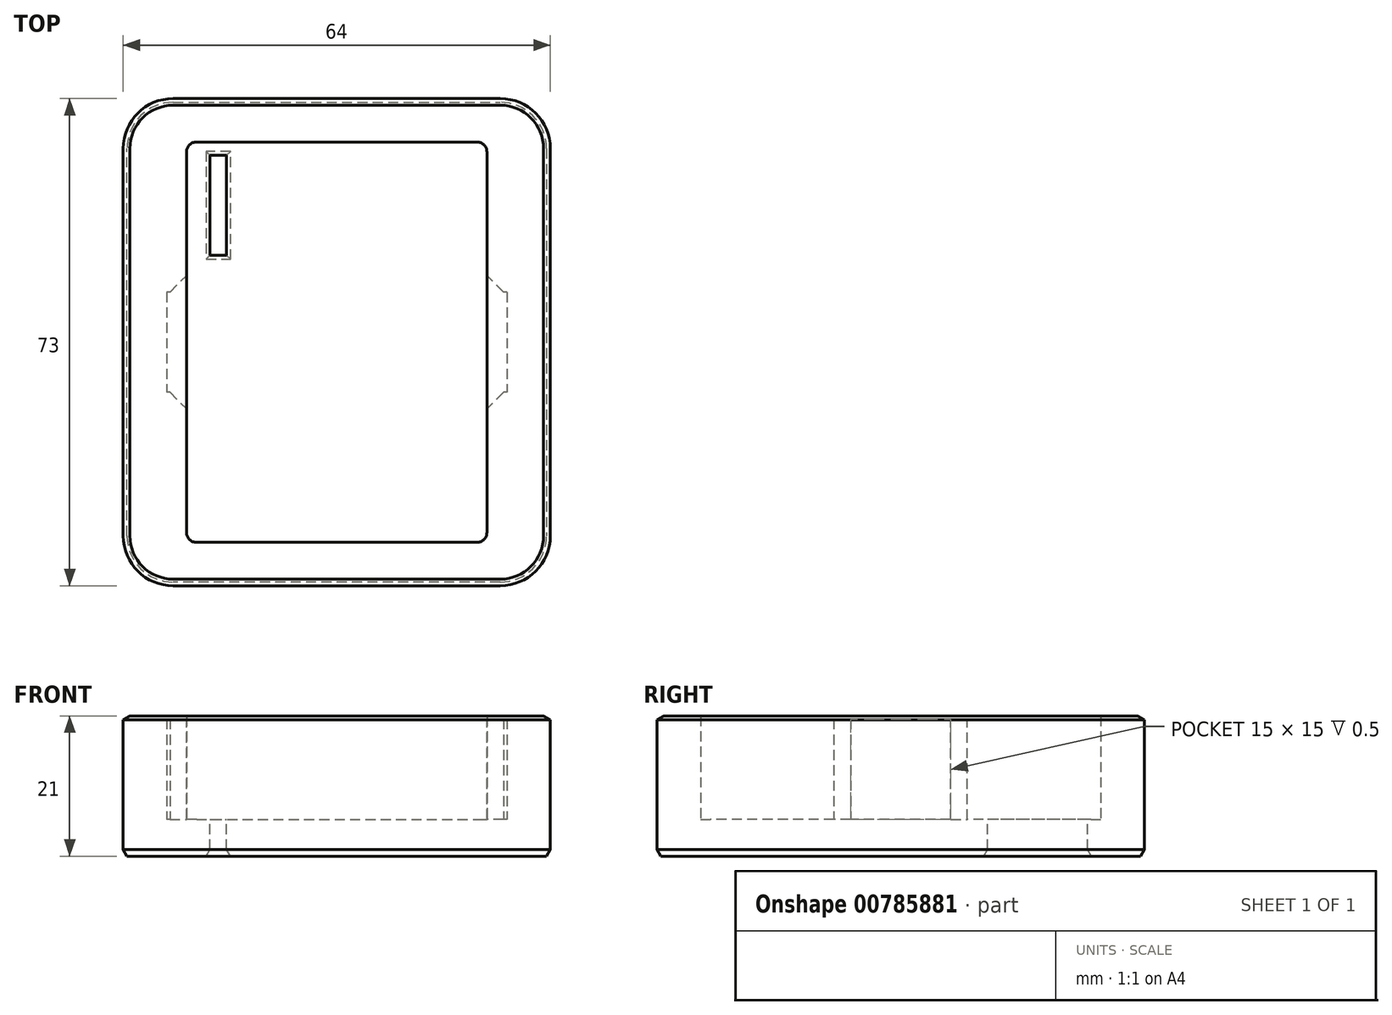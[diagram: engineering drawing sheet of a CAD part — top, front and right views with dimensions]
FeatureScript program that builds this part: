
annotation { "Feature Type Name" : "Feature", "Feature Type Description" : "" }
export const myFeature = defineFeature(function(context is Context, id is Id, definition is map)
    precondition{}
    {
        {
            var Q0;
            Q0=qCreatedBy(makeId("Top.planeOp"),FACE);
            var sketch = newSketch(context, id + "F0", { "sketchPlane" : qUnion([Q0])});
            skLineSegment(sketch, "E0.bottom", {"start": v(32, 36.5) * mm, "end": v(-32, 36.5) * mm});
            skLineSegment(sketch, "E0.top", {"start": v(32, -36.5) * mm, "end": v(-32, -36.5) * mm});
            skLineSegment(sketch, "E0.left", {"start": v(32, 36.5) * mm, "end": v(32, -36.5) * mm});
            skLineSegment(sketch, "E0.right", {"start": v(-32, 36.5) * mm, "end": v(-32, -36.5) * mm});
            skPoint(sketch, "E0.middle", {"position": v(0, 0) * mm});
            skLineSegment(sketch, "E1.bottom", {"start": v(-22.5, 30) * mm, "end": v(22.5, 30) * mm});
            skLineSegment(sketch, "E1.top", {"start": v(-22.5, -30) * mm, "end": v(22.5, -30) * mm});
            skLineSegment(sketch, "E1.left", {"start": v(-22.5, 30) * mm, "end": v(-22.5, 7.5) * mm});
            skLineSegment(sketch, "E1.right", {"start": v(22.5, 30) * mm, "end": v(22.5, 7.5) * mm});
            skLineSegment(sketch, "E2.bottom", {"start": v(25.5, 7.5) * mm, "end": v(22.5, 7.5) * mm});
            skLineSegment(sketch, "E2.top", {"start": v(25.5, -7.5) * mm, "end": v(22.5, -7.5) * mm});
            skLineSegment(sketch, "E2.left", {"start": v(25.5, 7.5) * mm, "end": v(25.5, -7.5) * mm});
            skLineSegment(sketch, "E2.right", {"start": v(-25.5, 7.5) * mm, "end": v(-25.5, -7.5) * mm});
            skLineSegment(sketch, "E3.trimOffspring", {"start": v(-22.5, 7.5) * mm, "end": v(-25.5, 7.5) * mm});
            skLineSegment(sketch, "E4.trimOffspring", {"start": v(-22.5, -7.5) * mm, "end": v(-25.5, -7.5) * mm});
            skLineSegment(sketch, "E5.trimOffspring", {"start": v(22.5, -7.5) * mm, "end": v(22.5, -30) * mm});
            skLineSegment(sketch, "E6.trimOffspring", {"start": v(-22.5, -7.5) * mm, "end": v(-22.5, -30) * mm});
            skSolve(sketch);
        }
        {
            var Q0;
            Q0=makeQuery(id+"F0.imprint","IMPRINT",FACE,{"disambiguationData":[TD([[makeQuery(id+"F0.imprint","IMPRINT",EDGE,{"derivedFrom":sQuery(id+"F0.wireOp",EDGE,"E0.bottom")}),1.0]])]});
            var Q1;
            Q1=makeQuery(id+"F0.imprint","IMPRINT",FACE,{"disambiguationData":[TD([[makeQuery(id+"F0.imprint","IMPRINT",EDGE,{"derivedFrom":sQuery(id+"F0.wireOp",EDGE,"E1.bottom")}),-1.0]])]});
            extrude(context, id + "F1", {"entities" : qUnion([Q0, Q1]), "oppositeDirection" : true, "depth" : (19 - 13.5) * mm, "offsetDistance" : 25 * mm});
        }
        {
            var Q0;
            Q0=makeQuery(id+"F0.imprint","IMPRINT",FACE,{"disambiguationData":[TD([[makeQuery(id+"F0.imprint","IMPRINT",EDGE,{"derivedFrom":sQuery(id+"F0.wireOp",EDGE,"E0.bottom")}),1.0]])]});
            extrude(context, id + "F2", {"entities" : qUnion([Q0]), "operationType" : NewBodyOperationType.ADD, "depth" : 15.5 * mm, "offsetDistance" : 25 * mm});
        }
        {
            var Q0;
            Q0=makeQuery(id+"F2.opExtrude","SWEPT_FACE",FACE,{"disambiguationData":[OSD([sQuery(id+"F0.wireOp",EDGE,"E2.right")])]});
            var sketch = newSketch(context, id + "F3", { "sketchPlane" : qUnion([Q0])});
            skLineSegment(sketch, "E7.bottom", {"start": v(-7.5, 15.5) * mm, "end": v(7.5, 15.5) * mm});
            skLineSegment(sketch, "E7.top", {"start": v(-7.5, 15) * mm, "end": v(7.5, 15) * mm});
            skLineSegment(sketch, "E7.left", {"start": v(-7.5, 15.5) * mm, "end": v(-7.5, 15) * mm});
            skLineSegment(sketch, "E7.right", {"start": v(7.5, 15.5) * mm, "end": v(7.5, 15) * mm});
            skSolve(sketch);
        }
        {
            var Q0;
            Q0 = qSketchRegion(id + "F3", true);
            var Q1;
            Q1=makeQuery(id+"F2.opExtrude","SWEPT_FACE",FACE,{"disambiguationData":[OSD([sQuery(id+"F0.wireOp",EDGE,"E6.trimOffspring")])]});
            extrude(context, id + "F4", {"entities" : qUnion([Q0]), "operationType" : NewBodyOperationType.ADD, "endBound" : BoundingType.UP_TO_SURFACE, "depth" : 25 * mm, "endBoundEntityFace" : qUnion([Q1]), "offsetDistance" : 25 * mm});
        }
        {
            var Q0;
            Q0=makeQuery(id+"F1.opExtrude","SWEPT_BODY",BODY,{"disambiguationData":[OSD([sQuery(id+"F0.wireOp",EDGE,"E0.bottom"),sQuery(id+"F0.wireOp",EDGE,"E0.top"),sQuery(id+"F0.wireOp",EDGE,"E0.left"),sQuery(id+"F0.wireOp",EDGE,"E0.right")])]});
            var Q1;
            Q1=qCreatedBy(makeId("Right.planeOp"),FACE);
            mirror(context, id + "F5", {"operationType" : NewBodyOperationType.ADD, "entities" : qUnion([Q0]), "mirrorPlane" : qUnion([Q1])});
        }
        {
            var Q0;
            Q0=makeQuery(id+"F1.opExtrude","CAP_FACE",FACE,{"disambiguationData":[OSD([sQuery(id+"F0.wireOp",EDGE,"E0.bottom"),sQuery(id+"F0.wireOp",EDGE,"E0.top"),sQuery(id+"F0.wireOp",EDGE,"E0.left"),sQuery(id+"F0.wireOp",EDGE,"E0.right")])],"isStart":true});
            var sketch = newSketch(context, id + "F6", { "sketchPlane" : qUnion([Q0])});
            skLineSegment(sketch, "E8.bottom", {"start": v(-19, 28) * mm, "end": v(-16.5, 28) * mm});
            skLineSegment(sketch, "E8.top", {"start": v(-19, 13) * mm, "end": v(-16.5, 13) * mm});
            skLineSegment(sketch, "E8.left", {"start": v(-19, 28) * mm, "end": v(-19, 13) * mm});
            skLineSegment(sketch, "E8.right", {"start": v(-16.5, 28) * mm, "end": v(-16.5, 13) * mm});
            skLineSegment(sketch, "E9.0", {"start": v(32, 36.5) * mm, "end": v(-32, 36.5) * mm});
            skLineSegment(sketch, "E10.0", {"start": v(-32, 36.5) * mm, "end": v(-32, -36.5) * mm});
            skSolve(sketch);
        }
        {
            var Q0;
            Q0 = qSketchRegion(id + "F6", true);
            extrude(context, id + "F7", {"entities" : qUnion([Q0]), "operationType" : NewBodyOperationType.REMOVE, "endBound" : BoundingType.THROUGH_ALL, "oppositeDirection" : true, "depth" : 25 * mm, "offsetDistance" : 25 * mm});
        }
        {
            var Q0;
            Q0=makeQuery(id+"F2.opExtrude","SWEPT_EDGE",EDGE,{"disambiguationData":[OSD([sQuery(id+"F0.wireOp",EDGE,"E4.trimOffspring"),sQuery(id+"F0.wireOp",EDGE,"E6.trimOffspring")])]});
            var Q1;
            Q1=makeQuery(id+"F2.opExtrude","SWEPT_EDGE",EDGE,{"disambiguationData":[OSD([sQuery(id+"F0.wireOp",EDGE,"E1.left"),sQuery(id+"F0.wireOp",EDGE,"E3.trimOffspring")])]});
            var Q2;
            Q2=makeQuery(id+"F2.opExtrude","SWEPT_EDGE",EDGE,{"disambiguationData":[OSD([sQuery(id+"F0.wireOp",EDGE,"E1.right"),sQuery(id+"F0.wireOp",EDGE,"E2.bottom")])]});
            var Q3;
            Q3=makeQuery(id+"F2.opExtrude","SWEPT_EDGE",EDGE,{"disambiguationData":[OSD([sQuery(id+"F0.wireOp",EDGE,"E2.top"),sQuery(id+"F0.wireOp",EDGE,"E5.trimOffspring")])]});
            chamfer(context, id + "F8", {"entities" : qUnion([Q0, Q1, Q2, Q3]), "width" : 2.5 * mm, "tangentPropagation" : true});
        }
        {
            var Q0;
            Q0=makeQuery(id+"F2.opExtrude","SWEPT_EDGE",EDGE,{"disambiguationData":[OSD([sQuery(id+"F0.wireOp",EDGE,"E1.bottom"),sQuery(id+"F0.wireOp",EDGE,"E1.left")])]});
            var Q1;
            Q1=makeQuery(id+"F2.opExtrude","SWEPT_EDGE",EDGE,{"disambiguationData":[OSD([sQuery(id+"F0.wireOp",EDGE,"E1.top"),sQuery(id+"F0.wireOp",EDGE,"E6.trimOffspring")])]});
            var Q2;
            Q2=makeQuery(id+"F2.opExtrude","SWEPT_EDGE",EDGE,{"disambiguationData":[OSD([sQuery(id+"F0.wireOp",EDGE,"E1.bottom"),sQuery(id+"F0.wireOp",EDGE,"E1.right")])]});
            var Q3;
            Q3=makeQuery(id+"F2.opExtrude","SWEPT_EDGE",EDGE,{"disambiguationData":[OSD([sQuery(id+"F0.wireOp",EDGE,"E1.top"),sQuery(id+"F0.wireOp",EDGE,"E5.trimOffspring")])]});
            fillet(context, id + "F9", {"entities" : qUnion([Q0, Q1, Q2, Q3]), "radius" : 1.5 * mm, "tangentPropagation" : true, "allowEdgeOverflow" : false});
        }
        {
            var Q0;
            {var subQ0=sQuery(id+"F0.wireOp",EDGE,"E0.right");var subQ1=sQuery(id+"F0.wireOp",EDGE,"E0.top");Q0=makeQuery(id+"F2.boolean.opBoolean","MERGE",EDGE,{"derivedFrom":[makeQuery(id+"F1.opExtrude","SWEPT_EDGE",EDGE,{"disambiguationData":[OSD([subQ1,subQ0])]}),makeQuery(id+"F2.opExtrude","SWEPT_EDGE",EDGE,{"disambiguationData":[OSD([subQ1,subQ0])]})]});}
            var Q1;
            {var subQ0=sQuery(id+"F0.wireOp",EDGE,"E0.left");var subQ1=sQuery(id+"F0.wireOp",EDGE,"E0.top");Q1=makeQuery(id+"F2.boolean.opBoolean","MERGE",EDGE,{"derivedFrom":[makeQuery(id+"F1.opExtrude","SWEPT_EDGE",EDGE,{"disambiguationData":[OSD([subQ1,subQ0])]}),makeQuery(id+"F2.opExtrude","SWEPT_EDGE",EDGE,{"disambiguationData":[OSD([subQ1,subQ0])]})]});}
            var Q2;
            {var subQ0=sQuery(id+"F0.wireOp",EDGE,"E0.right");var subQ1=sQuery(id+"F0.wireOp",EDGE,"E0.bottom");Q2=makeQuery(id+"F2.boolean.opBoolean","MERGE",EDGE,{"derivedFrom":[makeQuery(id+"F1.opExtrude","SWEPT_EDGE",EDGE,{"disambiguationData":[OSD([subQ1,subQ0])]}),makeQuery(id+"F2.opExtrude","SWEPT_EDGE",EDGE,{"disambiguationData":[OSD([subQ1,subQ0])]})]});}
            var Q3;
            {var subQ0=sQuery(id+"F0.wireOp",EDGE,"E0.left");var subQ1=sQuery(id+"F0.wireOp",EDGE,"E0.bottom");Q3=makeQuery(id+"F2.boolean.opBoolean","MERGE",EDGE,{"derivedFrom":[makeQuery(id+"F1.opExtrude","SWEPT_EDGE",EDGE,{"disambiguationData":[OSD([subQ1,subQ0])]}),makeQuery(id+"F2.opExtrude","SWEPT_EDGE",EDGE,{"disambiguationData":[OSD([subQ1,subQ0])]})]});}
            fillet(context, id + "F10", {"entities" : qUnion([Q0, Q1, Q2, Q3]), "radius" : 7.5 * mm, "tangentPropagation" : true, "allowEdgeOverflow" : false});
        }
        {
            var Q0;
            Q0=makeQuery(id+"F1.opExtrude","CAP_FACE",FACE,{"disambiguationData":[OSD([sQuery(id+"F0.wireOp",EDGE,"E0.bottom"),sQuery(id+"F0.wireOp",EDGE,"E0.top"),sQuery(id+"F0.wireOp",EDGE,"E0.left"),sQuery(id+"F0.wireOp",EDGE,"E0.right")])],"isStart":false});
            chamfer(context, id + "F11", {"entities" : qUnion([Q0]), "chamferType" : ChamferType.OFFSET_ANGLE, "width" : 1 * mm, "oppositeDirection" : false, "angle" : 30 * degree, "tangentPropagation" : true});
        }
        {
            var Q0;
            {var subQ0=sQuery(id+"F0.wireOp",EDGE,"E0.right");var subQ1=sQuery(id+"F0.wireOp",EDGE,"E0.top");var subQ2=makeQuery(id+"F4.boolean.opBoolean","MERGE",FACE,{"derivedFrom":[makeQuery(id+"F2.opExtrude","CAP_FACE",FACE,{"disambiguationData":[OSD([sQuery(id+"F0.wireOp",EDGE,"E0.bottom"),subQ1,sQuery(id+"F0.wireOp",EDGE,"E0.left"),subQ0,sQuery(id+"F0.wireOp",EDGE,"E1.bottom"),sQuery(id+"F0.wireOp",EDGE,"E1.top"),sQuery(id+"F0.wireOp",EDGE,"E1.left"),sQuery(id+"F0.wireOp",EDGE,"E1.right"),sQuery(id+"F0.wireOp",EDGE,"E2.bottom"),sQuery(id+"F0.wireOp",EDGE,"E2.top"),sQuery(id+"F0.wireOp",EDGE,"E2.left"),sQuery(id+"F0.wireOp",EDGE,"E2.right"),sQuery(id+"F0.wireOp",EDGE,"E3.trimOffspring"),sQuery(id+"F0.wireOp",EDGE,"E4.trimOffspring"),sQuery(id+"F0.wireOp",EDGE,"E5.trimOffspring"),sQuery(id+"F0.wireOp",EDGE,"E6.trimOffspring")])],"isStart":false}),makeQuery(id+"F4.opExtrude","SWEPT_FACE",FACE,{"disambiguationData":[OSD([sQuery(id+"F3.wireOp",EDGE,"E7.bottom")])]})]});Q0=makeQuery(id+"F10.opFillet","BLEND_EDGE",EDGE,{"blendedFrom":[makeQuery(id+"F2.boolean.opBoolean","MERGE",EDGE,{"derivedFrom":[makeQuery(id+"F1.opExtrude","SWEPT_EDGE",EDGE,{"disambiguationData":[OSD([subQ1,subQ0])]}),makeQuery(id+"F2.opExtrude","SWEPT_EDGE",EDGE,{"disambiguationData":[OSD([subQ1,subQ0])]})]}),makeQuery(id+"F5.boolean.opBoolean","MERGE",FACE,{"derivedFrom":[subQ2,makeQuery(id+"F5.opPattern","COPY",FACE,{"derivedFrom":subQ2,"instanceName":"1"})]})],"blendedInto":[makeQuery(id+"F5.boolean.opBoolean","MERGE",FACE,{"derivedFrom":[subQ2,makeQuery(id+"F5.opPattern","COPY",FACE,{"derivedFrom":subQ2,"instanceName":"1"})]})]});}
            var Q1;
            Q1=makeQuery(id+"F2.opExtrude","CAP_EDGE",EDGE,{"disambiguationData":[OSD([sQuery(id+"F0.wireOp",EDGE,"E0.right")])],"isStart":false});
            var Q2;
            Q2=makeQuery(id+"F2.opExtrude","CAP_EDGE",EDGE,{"disambiguationData":[OSD([sQuery(id+"F0.wireOp",EDGE,"E0.top")])],"isStart":false});
            var Q3;
            {var subQ0=sQuery(id+"F0.wireOp",EDGE,"E0.left");var subQ1=sQuery(id+"F0.wireOp",EDGE,"E0.top");var subQ2=makeQuery(id+"F4.boolean.opBoolean","MERGE",FACE,{"derivedFrom":[makeQuery(id+"F2.opExtrude","CAP_FACE",FACE,{"disambiguationData":[OSD([sQuery(id+"F0.wireOp",EDGE,"E0.bottom"),subQ1,subQ0,sQuery(id+"F0.wireOp",EDGE,"E0.right"),sQuery(id+"F0.wireOp",EDGE,"E1.bottom"),sQuery(id+"F0.wireOp",EDGE,"E1.top"),sQuery(id+"F0.wireOp",EDGE,"E1.left"),sQuery(id+"F0.wireOp",EDGE,"E1.right"),sQuery(id+"F0.wireOp",EDGE,"E2.bottom"),sQuery(id+"F0.wireOp",EDGE,"E2.top"),sQuery(id+"F0.wireOp",EDGE,"E2.left"),sQuery(id+"F0.wireOp",EDGE,"E2.right"),sQuery(id+"F0.wireOp",EDGE,"E3.trimOffspring"),sQuery(id+"F0.wireOp",EDGE,"E4.trimOffspring"),sQuery(id+"F0.wireOp",EDGE,"E5.trimOffspring"),sQuery(id+"F0.wireOp",EDGE,"E6.trimOffspring")])],"isStart":false}),makeQuery(id+"F4.opExtrude","SWEPT_FACE",FACE,{"disambiguationData":[OSD([sQuery(id+"F3.wireOp",EDGE,"E7.bottom")])]})]});Q3=makeQuery(id+"F10.opFillet","BLEND_EDGE",EDGE,{"blendedFrom":[makeQuery(id+"F2.boolean.opBoolean","MERGE",EDGE,{"derivedFrom":[makeQuery(id+"F1.opExtrude","SWEPT_EDGE",EDGE,{"disambiguationData":[OSD([subQ1,subQ0])]}),makeQuery(id+"F2.opExtrude","SWEPT_EDGE",EDGE,{"disambiguationData":[OSD([subQ1,subQ0])]})]}),makeQuery(id+"F5.boolean.opBoolean","MERGE",FACE,{"derivedFrom":[subQ2,makeQuery(id+"F5.opPattern","COPY",FACE,{"derivedFrom":subQ2,"instanceName":"1"})]})],"blendedInto":[makeQuery(id+"F5.boolean.opBoolean","MERGE",FACE,{"derivedFrom":[subQ2,makeQuery(id+"F5.opPattern","COPY",FACE,{"derivedFrom":subQ2,"instanceName":"1"})]})]});}
            var Q4;
            Q4=makeQuery(id+"F2.opExtrude","CAP_EDGE",EDGE,{"disambiguationData":[OSD([sQuery(id+"F0.wireOp",EDGE,"E0.left")])],"isStart":false});
            var Q5;
            {var subQ0=sQuery(id+"F0.wireOp",EDGE,"E0.left");var subQ1=sQuery(id+"F0.wireOp",EDGE,"E0.bottom");var subQ2=makeQuery(id+"F4.boolean.opBoolean","MERGE",FACE,{"derivedFrom":[makeQuery(id+"F2.opExtrude","CAP_FACE",FACE,{"disambiguationData":[OSD([subQ1,sQuery(id+"F0.wireOp",EDGE,"E0.top"),subQ0,sQuery(id+"F0.wireOp",EDGE,"E0.right"),sQuery(id+"F0.wireOp",EDGE,"E1.bottom"),sQuery(id+"F0.wireOp",EDGE,"E1.top"),sQuery(id+"F0.wireOp",EDGE,"E1.left"),sQuery(id+"F0.wireOp",EDGE,"E1.right"),sQuery(id+"F0.wireOp",EDGE,"E2.bottom"),sQuery(id+"F0.wireOp",EDGE,"E2.top"),sQuery(id+"F0.wireOp",EDGE,"E2.left"),sQuery(id+"F0.wireOp",EDGE,"E2.right"),sQuery(id+"F0.wireOp",EDGE,"E3.trimOffspring"),sQuery(id+"F0.wireOp",EDGE,"E4.trimOffspring"),sQuery(id+"F0.wireOp",EDGE,"E5.trimOffspring"),sQuery(id+"F0.wireOp",EDGE,"E6.trimOffspring")])],"isStart":false}),makeQuery(id+"F4.opExtrude","SWEPT_FACE",FACE,{"disambiguationData":[OSD([sQuery(id+"F3.wireOp",EDGE,"E7.bottom")])]})]});Q5=makeQuery(id+"F10.opFillet","BLEND_EDGE",EDGE,{"blendedFrom":[makeQuery(id+"F2.boolean.opBoolean","MERGE",EDGE,{"derivedFrom":[makeQuery(id+"F1.opExtrude","SWEPT_EDGE",EDGE,{"disambiguationData":[OSD([subQ1,subQ0])]}),makeQuery(id+"F2.opExtrude","SWEPT_EDGE",EDGE,{"disambiguationData":[OSD([subQ1,subQ0])]})]}),makeQuery(id+"F5.boolean.opBoolean","MERGE",FACE,{"derivedFrom":[subQ2,makeQuery(id+"F5.opPattern","COPY",FACE,{"derivedFrom":subQ2,"instanceName":"1"})]})],"blendedInto":[makeQuery(id+"F5.boolean.opBoolean","MERGE",FACE,{"derivedFrom":[subQ2,makeQuery(id+"F5.opPattern","COPY",FACE,{"derivedFrom":subQ2,"instanceName":"1"})]})]});}
            var Q6;
            Q6=makeQuery(id+"F2.opExtrude","CAP_EDGE",EDGE,{"disambiguationData":[OSD([sQuery(id+"F0.wireOp",EDGE,"E0.bottom")])],"isStart":false});
            var Q7;
            {var subQ0=sQuery(id+"F0.wireOp",EDGE,"E0.right");var subQ1=sQuery(id+"F0.wireOp",EDGE,"E0.bottom");var subQ2=makeQuery(id+"F4.boolean.opBoolean","MERGE",FACE,{"derivedFrom":[makeQuery(id+"F2.opExtrude","CAP_FACE",FACE,{"disambiguationData":[OSD([subQ1,sQuery(id+"F0.wireOp",EDGE,"E0.top"),sQuery(id+"F0.wireOp",EDGE,"E0.left"),subQ0,sQuery(id+"F0.wireOp",EDGE,"E1.bottom"),sQuery(id+"F0.wireOp",EDGE,"E1.top"),sQuery(id+"F0.wireOp",EDGE,"E1.left"),sQuery(id+"F0.wireOp",EDGE,"E1.right"),sQuery(id+"F0.wireOp",EDGE,"E2.bottom"),sQuery(id+"F0.wireOp",EDGE,"E2.top"),sQuery(id+"F0.wireOp",EDGE,"E2.left"),sQuery(id+"F0.wireOp",EDGE,"E2.right"),sQuery(id+"F0.wireOp",EDGE,"E3.trimOffspring"),sQuery(id+"F0.wireOp",EDGE,"E4.trimOffspring"),sQuery(id+"F0.wireOp",EDGE,"E5.trimOffspring"),sQuery(id+"F0.wireOp",EDGE,"E6.trimOffspring")])],"isStart":false}),makeQuery(id+"F4.opExtrude","SWEPT_FACE",FACE,{"disambiguationData":[OSD([sQuery(id+"F3.wireOp",EDGE,"E7.bottom")])]})]});Q7=makeQuery(id+"F10.opFillet","BLEND_EDGE",EDGE,{"blendedFrom":[makeQuery(id+"F2.boolean.opBoolean","MERGE",EDGE,{"derivedFrom":[makeQuery(id+"F1.opExtrude","SWEPT_EDGE",EDGE,{"disambiguationData":[OSD([subQ1,subQ0])]}),makeQuery(id+"F2.opExtrude","SWEPT_EDGE",EDGE,{"disambiguationData":[OSD([subQ1,subQ0])]})]}),makeQuery(id+"F5.boolean.opBoolean","MERGE",FACE,{"derivedFrom":[subQ2,makeQuery(id+"F5.opPattern","COPY",FACE,{"derivedFrom":subQ2,"instanceName":"1"})]})],"blendedInto":[makeQuery(id+"F5.boolean.opBoolean","MERGE",FACE,{"derivedFrom":[subQ2,makeQuery(id+"F5.opPattern","COPY",FACE,{"derivedFrom":subQ2,"instanceName":"1"})]})]});}
            chamfer(context, id + "F12", {"entities" : qUnion([Q0, Q1, Q2, Q3, Q4, Q5, Q6, Q7]), "chamferType" : ChamferType.OFFSET_ANGLE, "width" : 1 * mm, "oppositeDirection" : false, "angle" : 30 * degree, "tangentPropagation" : true});
        }
    });
